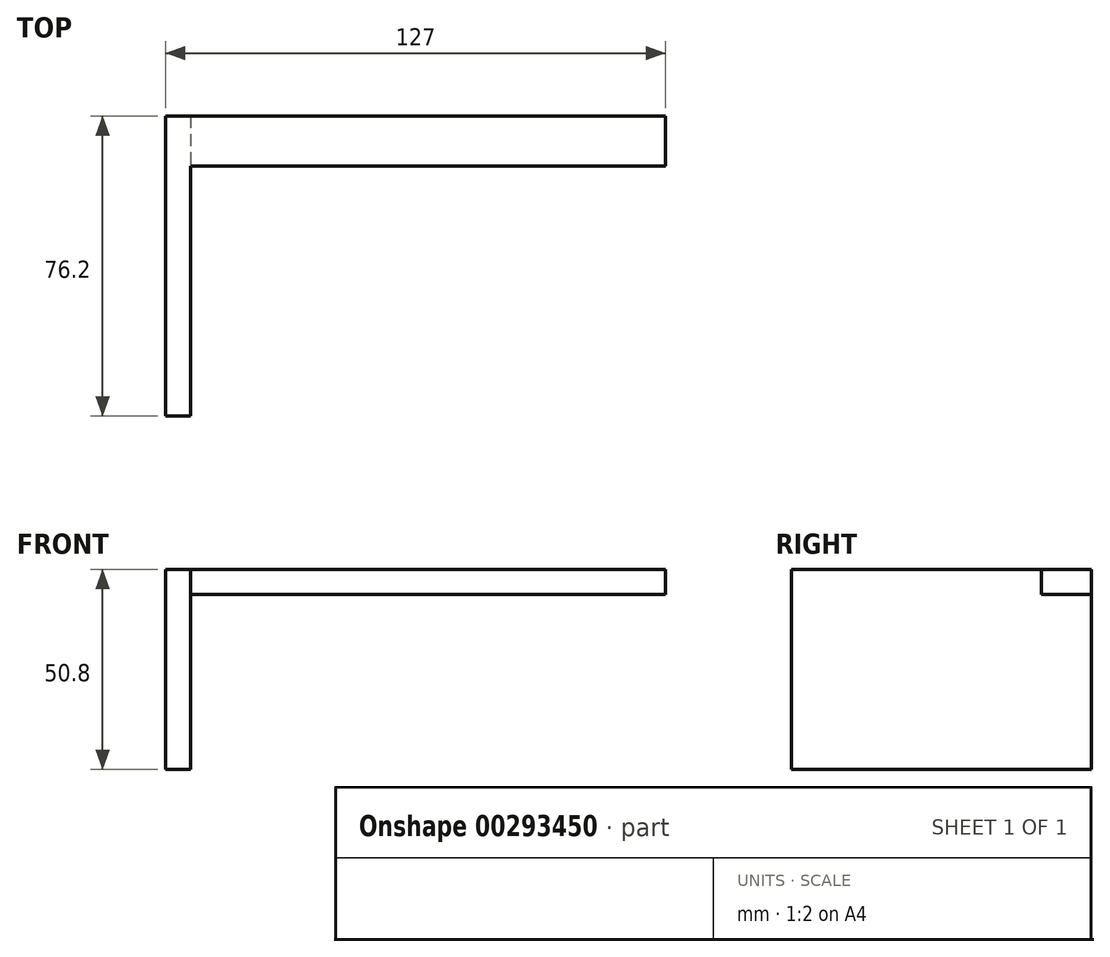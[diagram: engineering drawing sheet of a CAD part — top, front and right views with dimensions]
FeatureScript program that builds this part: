
annotation { "Feature Type Name" : "Feature", "Feature Type Description" : "" }
export const myFeature = defineFeature(function(context is Context, id is Id, definition is map)
    precondition{}
    {
        {
            var Q0;
            Q0=qCreatedBy(makeId("Top.planeOp"),FACE);
            var sketch = newSketch(context, id + "F0", { "sketchPlane" : qUnion([Q0])});
            skLineSegment(sketch, "E0.bottom", {"start": v(0, 0) * mm, "end": v(127, 0) * mm});
            skLineSegment(sketch, "E0.top", {"start": v(0, 12.7) * mm, "end": v(127, 12.7) * mm});
            skLineSegment(sketch, "E0.left", {"start": v(0, 0) * mm, "end": v(0, 12.7) * mm});
            skLineSegment(sketch, "E0.right", {"start": v(127, 0) * mm, "end": v(127, 12.7) * mm});
            skSolve(sketch);
        }
        {
            var Q0;
            Q0 = qSketchRegion(id + "F0", true);
            extrude(context, id + "F1", {"entities" : qUnion([Q0]), "depth" : 6.35 * mm});
        }
        {
            var Q0;
            Q0=makeQuery(id+"F1.opExtrude","CAP_FACE",FACE,{"disambiguationData":[OSD([sQuery(id+"F0.wireOp",EDGE,"E0.bottom"),sQuery(id+"F0.wireOp",EDGE,"E0.top"),sQuery(id+"F0.wireOp",EDGE,"E0.left"),sQuery(id+"F0.wireOp",EDGE,"E0.right")])],"isStart":false});
            var sketch = newSketch(context, id + "F2", { "sketchPlane" : qUnion([Q0])});
            skLineSegment(sketch, "E1.bottom", {"start": v(0, 12.7) * mm, "end": v(6.35, 12.7) * mm});
            skLineSegment(sketch, "E1.top", {"start": v(0, -63.5) * mm, "end": v(6.35, -63.5) * mm});
            skLineSegment(sketch, "E1.left", {"start": v(0, 12.7) * mm, "end": v(0, -63.5) * mm});
            skLineSegment(sketch, "E1.right", {"start": v(6.35, 12.7) * mm, "end": v(6.35, -63.5) * mm});
            skSolve(sketch);
        }
        {
            var Q0;
            Q0 = qSketchRegion(id + "F2", true);
            extrude(context, id + "F3", {"entities" : qUnion([Q0]), "operationType" : NewBodyOperationType.ADD, "oppositeDirection" : true, "depth" : 50.8 * mm});
        }
    });
